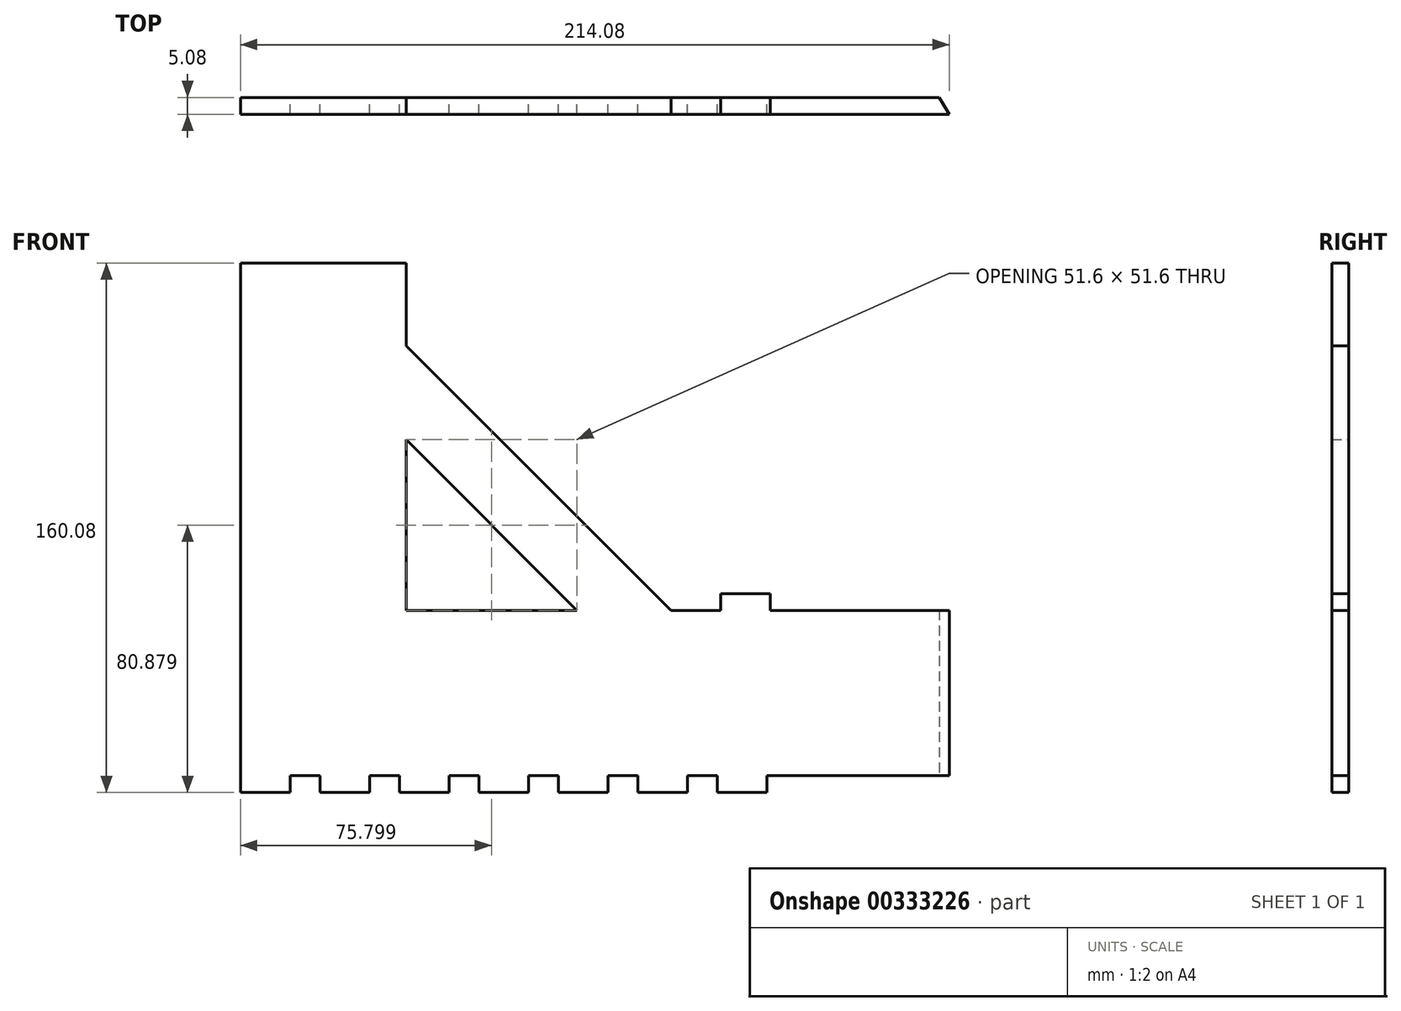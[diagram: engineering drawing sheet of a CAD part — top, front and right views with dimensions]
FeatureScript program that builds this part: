
annotation { "Feature Type Name" : "Feature", "Feature Type Description" : "" }
export const myFeature = defineFeature(function(context is Context, id is Id, definition is map)
    precondition{}
    {
        {
            var Q0;
            Q0=qCreatedBy(makeId("Front.planeOp"),FACE);
            var sketch = newSketch(context, id + "F0", { "sketchPlane" : qUnion([Q0])});
            skLineSegment(sketch, "E0", {"start": v(-32.42, 0) * mm, "end": v(-246.5, 0) * mm});
            skLineSegment(sketch, "E1", {"start": v(-246.5, 0) * mm, "end": v(-246.5, 130) * mm});
            skLineSegment(sketch, "E2", {"start": v(-246.5, 130) * mm, "end": v(-196.5, 130) * mm});
            skLineSegment(sketch, "E3", {"start": v(-196.5, 130) * mm, "end": v(-196.5, 50) * mm});
            skLineSegment(sketch, "E4", {"start": v(-196.5, 50) * mm, "end": v(-32.42, 50) * mm});
            skLineSegment(sketch, "E5", {"start": v(-196.5, 130) * mm, "end": v(-116.5, 50) * mm});
            skLineSegment(sketch, "E6", {"start": v(-196.5, 101.6) * mm, "end": v(-144.9, 50) * mm});
            skLineSegment(sketch, "E7", {"start": v(-246.5, 0) * mm, "end": v(-246.5, -5.08) * mm});
            skLineSegment(sketch, "E8", {"start": v(-246.5, -5.08) * mm, "end": v(-231.5, -5.08) * mm});
            skLineSegment(sketch, "E9", {"start": v(-231.5, -5.08) * mm, "end": v(-231.5, 0) * mm});
            skLineSegment(sketch, "E10.1.0.0", {"start": v(-207.5, -5.08) * mm, "end": v(-207.5, 0) * mm});
            skLineSegment(sketch, "E10.1.0.1", {"start": v(-222.5, -5.08) * mm, "end": v(-207.5, -5.08) * mm});
            skLineSegment(sketch, "E10.1.0.2", {"start": v(-222.5, 0) * mm, "end": v(-222.5, -5.08) * mm});
            skLineSegment(sketch, "E10.2.0.0", {"start": v(-183.5, -5.08) * mm, "end": v(-183.5, 0) * mm});
            skLineSegment(sketch, "E10.2.0.1", {"start": v(-198.5, -5.08) * mm, "end": v(-183.5, -5.08) * mm});
            skLineSegment(sketch, "E10.2.0.2", {"start": v(-198.5, 0) * mm, "end": v(-198.5, -5.08) * mm});
            skLineSegment(sketch, "E10.3.0.0", {"start": v(-159.5, -5.08) * mm, "end": v(-159.5, 0) * mm});
            skLineSegment(sketch, "E10.3.0.1", {"start": v(-174.5, -5.08) * mm, "end": v(-159.5, -5.08) * mm});
            skLineSegment(sketch, "E10.3.0.2", {"start": v(-174.5, 0) * mm, "end": v(-174.5, -5.08) * mm});
            skLineSegment(sketch, "E10.4.0.0", {"start": v(-135.5, -5.08) * mm, "end": v(-135.5, 0) * mm});
            skLineSegment(sketch, "E10.4.0.1", {"start": v(-150.5, -5.08) * mm, "end": v(-135.5, -5.08) * mm});
            skLineSegment(sketch, "E10.4.0.2", {"start": v(-150.5, 0) * mm, "end": v(-150.5, -5.08) * mm});
            skLineSegment(sketch, "E10.5.0.0", {"start": v(-111.5, -5.08) * mm, "end": v(-111.5, 0) * mm});
            skLineSegment(sketch, "E10.5.0.1", {"start": v(-126.5, -5.08) * mm, "end": v(-111.5, -5.08) * mm});
            skLineSegment(sketch, "E10.5.0.2", {"start": v(-126.5, 0) * mm, "end": v(-126.5, -5.08) * mm});
            skLineSegment(sketch, "E10.6.0.0", {"start": v(-87.5, -5.08) * mm, "end": v(-87.5, 0) * mm});
            skLineSegment(sketch, "E10.6.0.1", {"start": v(-102.5, -5.08) * mm, "end": v(-87.5, -5.08) * mm});
            skLineSegment(sketch, "E10.6.0.2", {"start": v(-102.5, 0) * mm, "end": v(-102.5, -5.08) * mm});
            skLineSegment(sketch, "E10.direction1", {"start": v(-246.5, -5.08) * mm, "end": v(-222.5, -5.08) * mm, "construction": true});
            skLineSegment(sketch, "E11", {"start": v(-32.42, 50) * mm, "end": v(-32.42, 0) * mm});
            skPoint(sketch, "E12.start.orphan", {"position": v(0, 50) * mm});
            skSolve(sketch);
        }
        {
            var Q0;
            Q0=qSketchRegion(id+"F0",true);
            extrude(context, id + "F1", {"entities" : qUnion([Q0]), "depth" : 5.08 * mm});
        }
        {
            var Q0;
            Q0=makeQuery(id+"F1.opExtrude","SWEPT_FACE",FACE,{"disambiguationData":[OSD([sQuery(id+"F0.wireOp",EDGE,"E2")])]});
            var Q1;
            Q1=makeQuery(id+"F1.opExtrude","SWEPT_FACE",FACE,{"disambiguationData":[OSD([sQuery(id+"F0.wireOp",EDGE,"0f3f7d79-0024-4810-854d-b7a6c9fa19c64.MirrorCS")])]});
            extrude(context, id + "F2", {"entities" : qUnion([Q0, Q1]), "operationType" : NewBodyOperationType.ADD, "depth" : 25 * mm});
        }
        {
            var Q0;
            {var subQ0=sQuery(id+"F0.wireOp",EDGE,"E0");Q0=makeQuery(id+"F1.opExtrude","SWEPT_FACE",FACE,{"disambiguationData":[OSD([subQ0]),TDD([makeQuery(id+"F0.imprint","IMPRINT",EDGE,{"disambiguationData":[TD([[makeQuery(id+"F0.imprint","INTERSECT",VERTEX,{"derivedFrom":[subQ0,sQuery(id+"F0.wireOp",EDGE,"E11")]}),-1.0]])],"derivedFrom":subQ0})])]});}
            var sketch = newSketch(context, id + "F3", { "sketchPlane" : qUnion([Q0])});
            skLineSegment(sketch, "E13", {"start": v(-32.42, 5.08) * mm, "end": v(-35.35, 0) * mm});
            skSolve(sketch);
        }
        {
            var Q0;
            {var subQ0=sQuery(id+"F3.wireOp",EDGE,"E13");Q0=makeQuery(id+"F3.imprint","IMPRINT",FACE,{"disambiguationData":[TD([[makeQuery(id+"F3.imprint","IMPRINT",EDGE,{"derivedFrom":subQ0}),1.0]])]});}
            extrude(context, id + "F4", {"entities" : qUnion([Q0]), "operationType" : NewBodyOperationType.REMOVE, "oppositeDirection" : true, "depth" : 58 * mm});
        }
        {
            var Q0;
            {var subQ0=sQuery(id+"F0.wireOp",EDGE,"E4");Q0=makeQuery(id+"F1.opExtrude","SWEPT_FACE",FACE,{"disambiguationData":[OSD([subQ0]),TDD([makeQuery(id+"F0.imprint","IMPRINT",EDGE,{"disambiguationData":[TD([[makeQuery(id+"F0.imprint","INTERSECT",VERTEX,{"derivedFrom":[subQ0,sQuery(id+"F0.wireOp",EDGE,"E11")]}),1.0]])],"derivedFrom":subQ0})])]});}
            var sketch = newSketch(context, id + "F5", { "sketchPlane" : qUnion([Q0])});
            skLineSegment(sketch, "E14.right", {"start": v(-101.5, 0) * mm, "end": v(-101.5, -5.08) * mm});
            skLineSegment(sketch, "E15.MirrorCS", {"start": v(-86.5, 0) * mm, "end": v(-86.5, -5.08) * mm});
            skPoint(sketch, "E14.top.start.orphan", {"position": v(-116.5, -5.08) * mm});
            skPoint(sketch, "E14.bottom.start.orphan", {"position": v(-116.5, 0) * mm});
            skLineSegment(sketch, "E16", {"start": v(-101.5, 0) * mm, "end": v(-86.5, 0) * mm});
            skLineSegment(sketch, "E17", {"start": v(-86.5, -5.08) * mm, "end": v(-101.5, -5.08) * mm});
            skSolve(sketch);
        }
        {
            var Q0;
            Q0=qSketchRegion(id+"F5",true);
            extrude(context, id + "F6", {"entities" : qUnion([Q0]), "operationType" : NewBodyOperationType.ADD, "depth" : 5.08 * mm});
        }
    });
